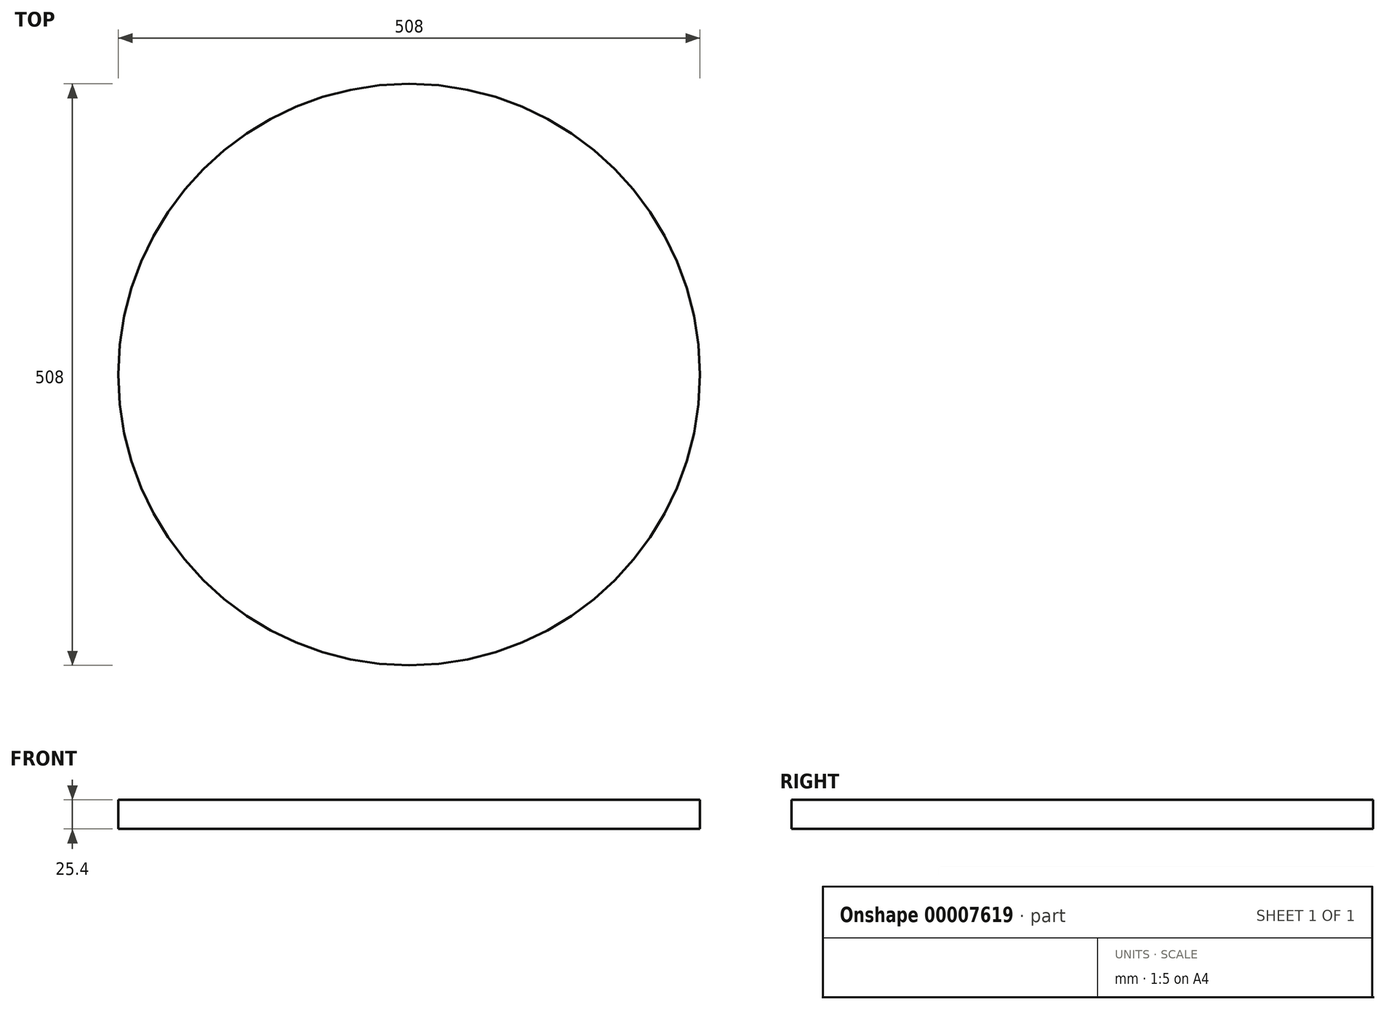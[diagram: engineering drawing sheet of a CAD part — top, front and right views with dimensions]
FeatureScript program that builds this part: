
annotation { "Feature Type Name" : "Feature", "Feature Type Description" : "" }
export const myFeature = defineFeature(function(context is Context, id is Id, definition is map)
    precondition{}
    {
        {
            var Q0;
            Q0=qCreatedBy(makeId("Top.planeOp"),FACE);
            var sketch = newSketch(context, id + "F0", { "sketchPlane" : qUnion([Q0])});
            skCircle(sketch, "E0", {"center": v(0, 0) * mm, "radius": 254 * mm});
            skSolve(sketch);
        }
        {
            var Q0;
            Q0=makeQuery(id+"F0.imprint","IMPRINT",FACE,{"disambiguationData":[TD([[makeQuery(id+"F0.imprint","IMPRINT",EDGE,{"derivedFrom":sQuery(id+"F0.wireOp",EDGE,"E0")}),1.0]])]});
            extrude(context, id + "F1", {"entities" : qUnion([Q0]), "depth" : 25.4 * mm});
        }
    });
